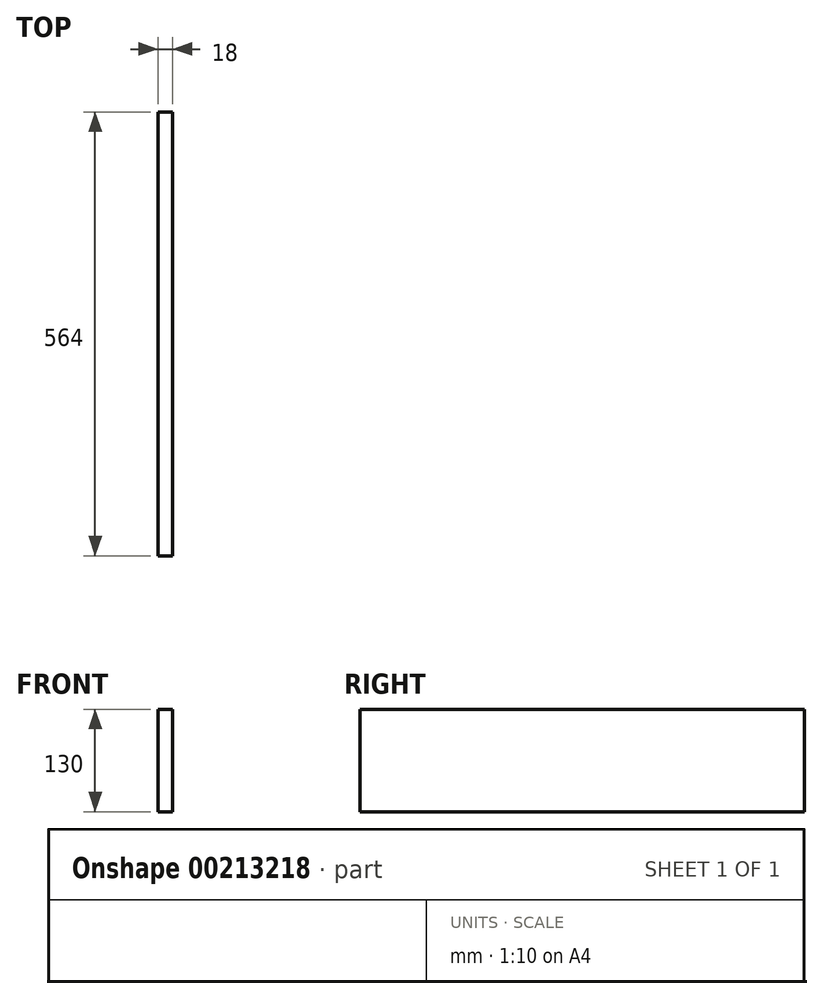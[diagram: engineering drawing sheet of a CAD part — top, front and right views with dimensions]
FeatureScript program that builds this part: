
annotation { "Feature Type Name" : "Feature", "Feature Type Description" : "" }
export const myFeature = defineFeature(function(context is Context, id is Id, definition is map)
    precondition{}
    {
        {
            var Q0;
            Q0=qCreatedBy(makeId("Right.planeOp"),FACE);
            var sketch = newSketch(context, id + "F0", { "sketchPlane" : qUnion([Q0])});
            skLineSegment(sketch, "E0.bottom", {"start": v(-282, 65) * mm, "end": v(282, 65) * mm});
            skLineSegment(sketch, "E0.top", {"start": v(-282, -65) * mm, "end": v(282, -65) * mm});
            skLineSegment(sketch, "E0.left", {"start": v(-282, 65) * mm, "end": v(-282, -65) * mm});
            skLineSegment(sketch, "E0.right", {"start": v(282, 65) * mm, "end": v(282, -65) * mm});
            skPoint(sketch, "E0.middle", {"position": v(0, 0) * mm});
            skSolve(sketch);
        }
        {
            var Q0;
            Q0=makeQuery(id+"F0.imprint","IMPRINT",FACE,{"disambiguationData":[TD([[makeQuery(id+"F0.imprint","IMPRINT",EDGE,{"derivedFrom":sQuery(id+"F0.wireOp",EDGE,"E0.bottom")}),-1.0]])]});
            extrude(context, id + "F1", {"entities" : qUnion([Q0]), "endBound" : BoundingType.SYMMETRIC, "depth" : 18 * mm});
        }
    });
